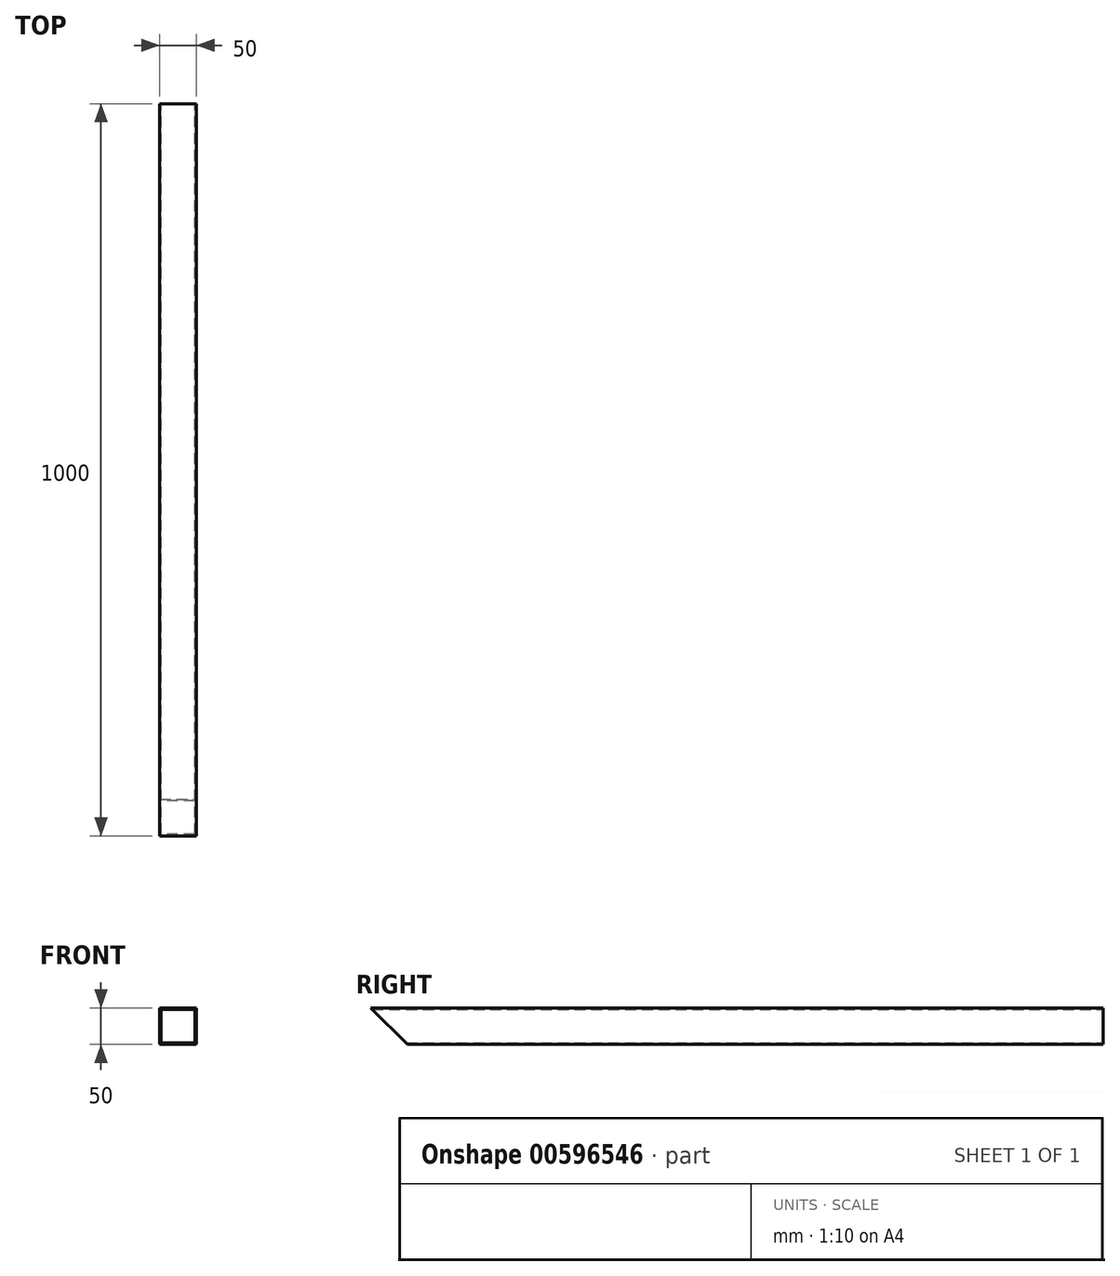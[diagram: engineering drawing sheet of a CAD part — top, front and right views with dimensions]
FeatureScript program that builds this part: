
annotation { "Feature Type Name" : "Feature", "Feature Type Description" : "" }
export const myFeature = defineFeature(function(context is Context, id is Id, definition is map)
    precondition{}
    {
        {
            var Q0;
            Q0=qCreatedBy(makeId("Front.planeOp"),FACE);
            var sketch = newSketch(context, id + "F0", { "sketchPlane" : qUnion([Q0])});
            skLineSegment(sketch, "E0.bottom", {"start": v(0, 0) * mm, "end": v(50, 0) * mm});
            skLineSegment(sketch, "E0.top", {"start": v(0, 50) * mm, "end": v(50, 50) * mm});
            skLineSegment(sketch, "E0.left", {"start": v(0, 0) * mm, "end": v(0, 50) * mm});
            skLineSegment(sketch, "E0.right", {"start": v(50, 0) * mm, "end": v(50, 50) * mm});
            skLineSegment(sketch, "E1.bottom", {"start": v(2, 2) * mm, "end": v(48, 2) * mm});
            skLineSegment(sketch, "E1.top", {"start": v(2, 48) * mm, "end": v(48, 48) * mm});
            skLineSegment(sketch, "E1.left", {"start": v(2, 2) * mm, "end": v(2, 48) * mm});
            skLineSegment(sketch, "E1.right", {"start": v(48, 2) * mm, "end": v(48, 48) * mm});
            skSolve(sketch);
        }
        {
            var Q0;
            Q0=makeQuery(id+"F0.imprint","IMPRINT",FACE,{"disambiguationData":[TD([[makeQuery(id+"F0.imprint","IMPRINT",EDGE,{"derivedFrom":sQuery(id+"F0.wireOp",EDGE,"E0.bottom")}),1.0]])]});
            extrude(context, id + "F1", {"entities" : qUnion([Q0]), "depth" : 1000 * mm, "offsetDistance" : 25 * mm});
        }
        {
            var Q0;
            Q0=makeQuery(id+"F1.opExtrude","SWEPT_FACE",FACE,{"disambiguationData":[OSD([sQuery(id+"F0.wireOp",EDGE,"E0.right")])]});
            var sketch = newSketch(context, id + "F2", { "sketchPlane" : qUnion([Q0])});
            skLineSegment(sketch, "E2", {"start": v(-1000, 50) * mm, "end": v(-1000, 0) * mm});
            skLineSegment(sketch, "E3", {"start": v(-1000, 0) * mm, "end": v(-950, 0) * mm});
            skLineSegment(sketch, "E4", {"start": v(-950, 0) * mm, "end": v(-1000, 50) * mm});
            skSolve(sketch);
        }
        {
            var Q0;
            Q0=makeQuery(id+"F2.imprint","IMPRINT",FACE,{"disambiguationData":[TD([[makeQuery(id+"F2.imprint","IMPRINT",EDGE,{"derivedFrom":sQuery(id+"F2.wireOp",EDGE,"E2")}),-1.0]])]});
            extrude(context, id + "F3", {"entities" : qUnion([Q0]), "operationType" : NewBodyOperationType.REMOVE, "endBound" : BoundingType.THROUGH_ALL, "oppositeDirection" : true, "depth" : 25 * mm, "offsetDistance" : 25 * mm});
        }
        {
            var Q0;
            Q0=makeQuery(id+"F1.opExtrude","CAP_FACE",FACE,{"disambiguationData":[OSD([sQuery(id+"F0.wireOp",EDGE,"E0.bottom"),sQuery(id+"F0.wireOp",EDGE,"E0.top"),sQuery(id+"F0.wireOp",EDGE,"E0.left"),sQuery(id+"F0.wireOp",EDGE,"E0.right"),sQuery(id+"F0.wireOp",EDGE,"E1.bottom"),sQuery(id+"F0.wireOp",EDGE,"E1.top"),sQuery(id+"F0.wireOp",EDGE,"E1.left"),sQuery(id+"F0.wireOp",EDGE,"E1.right")])],"isStart":true});
            cPlane(context, id + "F4", {"entities" : qUnion([Q0]), "cplaneType" : CPlaneType.OFFSET, "offset" : 500 * mm, "oppositeDirection" : true, "width" : 150 * mm, "height" : 150 * mm});
        }
    });
